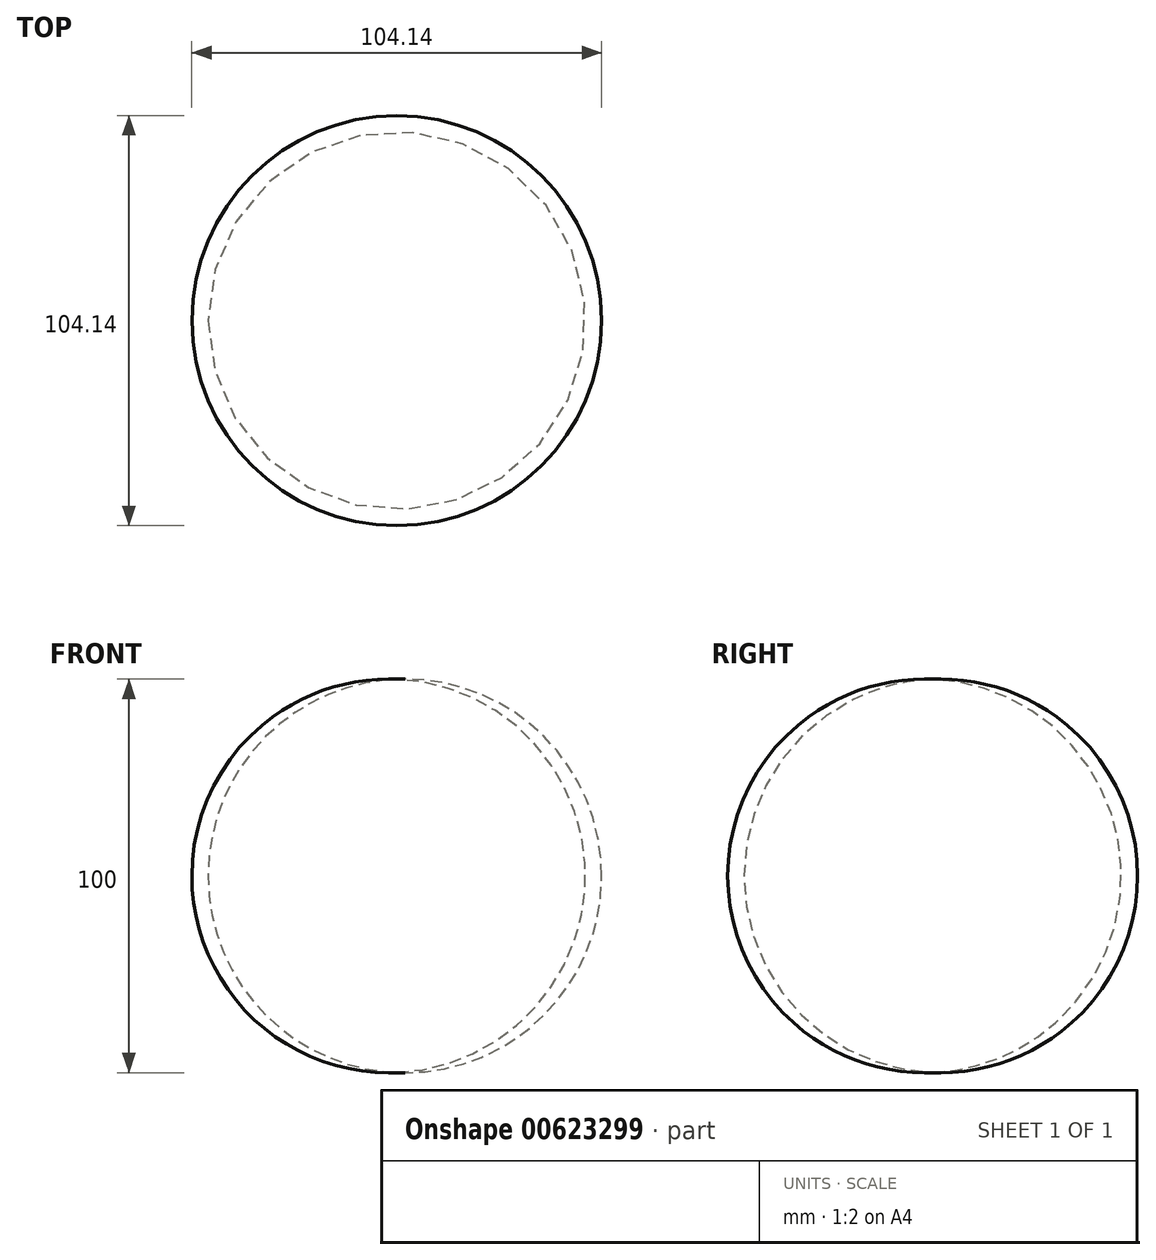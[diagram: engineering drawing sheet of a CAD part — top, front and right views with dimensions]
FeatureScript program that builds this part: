
annotation { "Feature Type Name" : "Feature", "Feature Type Description" : "" }
export const myFeature = defineFeature(function(context is Context, id is Id, definition is map)
    precondition{}
    {
        {
            var Q0;
            Q0=qCreatedBy(makeId("Top.planeOp"),FACE);
            var sketch = newSketch(context, id + "F0", { "sketchPlane" : qUnion([Q0])});
            skCircle(sketch, "E0", {"center": v(0, 0) * mm, "radius": 50 * mm});
            skSolve(sketch);
        }
        {
            var Q0;
            Q0=qCreatedBy(makeId("Front.planeOp"),FACE);
            var sketch = newSketch(context, id + "F1", { "sketchPlane" : qUnion([Q0])});
            skLineSegment(sketch, "E1", {"start": v(0, 0) * mm, "end": v(0, 49.96) * mm});
            skLineSegment(sketch, "E2", {"start": v(0, 0) * mm, "end": v(0, -49.96) * mm});
            skArc(sketch, "E3", {"start": v(0, 49.96) * mm, "mid": v(-52.07, 0) * mm, "end": v(0, -49.96) * mm});
            skSolve(sketch);
        }
        {
            var Q0;
            Q0=makeQuery(id+"F1.imprint","IMPRINT",FACE,{"disambiguationData":[TD([[makeQuery(id+"F1.imprint","IMPRINT",EDGE,{"derivedFrom":sQuery(id+"F1.wireOp",EDGE,"E1")}),1.0]])]});
            var Q1;
            Q1=sQuery(id+"F0.wireOp",EDGE,"E0");
            sweep(context, id + "F2", {"profiles" : qUnion([Q0]), "path" : qUnion([Q1])});
        }
    });
